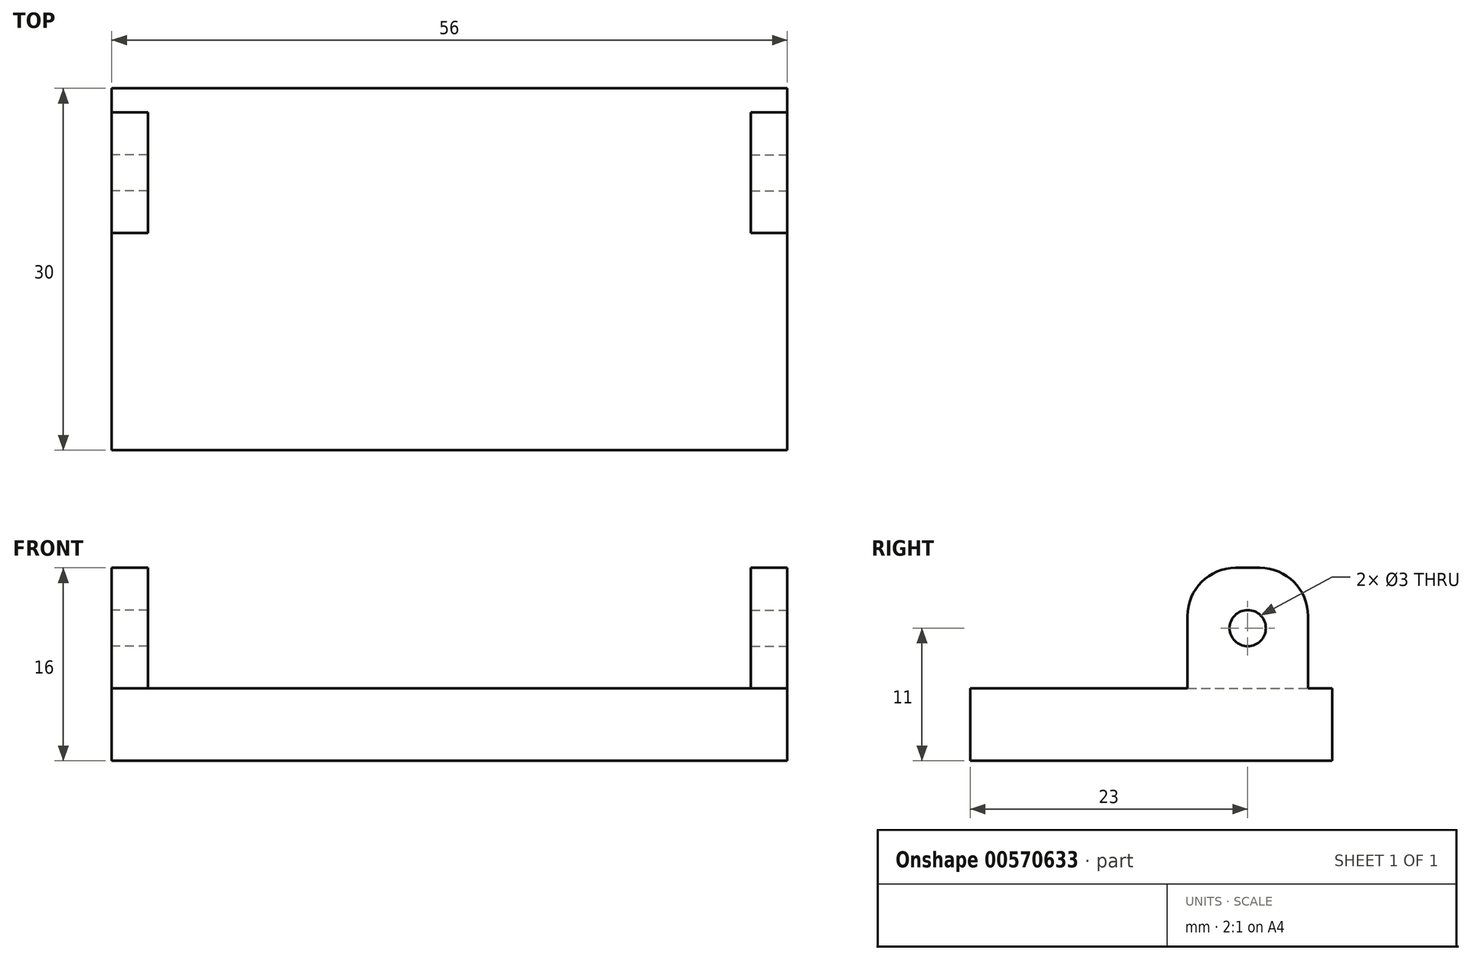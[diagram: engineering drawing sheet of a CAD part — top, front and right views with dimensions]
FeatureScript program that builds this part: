
annotation { "Feature Type Name" : "Feature", "Feature Type Description" : "" }
export const myFeature = defineFeature(function(context is Context, id is Id, definition is map)
    precondition{}
    {
        {
            var Q0;
            Q0=qCreatedBy(makeId("Top.planeOp"),FACE);
            var sketch = newSketch(context, id + "F0", { "sketchPlane" : qUnion([Q0])});
            skLineSegment(sketch, "E0.bottom", {"start": v(14, -15) * mm, "end": v(-14, -15) * mm});
            skLineSegment(sketch, "E0.top", {"start": v(14, 15) * mm, "end": v(-14, 15) * mm});
            skLineSegment(sketch, "E0.left", {"start": v(14, -15) * mm, "end": v(14, 15) * mm});
            skLineSegment(sketch, "E0.right", {"start": v(-14, -15) * mm, "end": v(-14, 15) * mm});
            skPoint(sketch, "E0.middle", {"position": v(0, 0) * mm});
            skSolve(sketch);
        }
        {
            var Q0;
            Q0 = qSketchRegion(id + "F0", true);
            extrude(context, id + "F1", {"entities" : qUnion([Q0]), "depth" : 6 * mm, "offsetDistance" : 25 * mm});
        }
        {
            var Q0;
            Q0=makeQuery(id+"F1.opExtrude","SWEPT_FACE",FACE,{"disambiguationData":[OSD([sQuery(id+"F0.wireOp",EDGE,"E0.left")])]});
            var sketch = newSketch(context, id + "F2", { "sketchPlane" : qUnion([Q0])});
            skLineSegment(sketch, "E1.bottom", {"start": v(13, 6) * mm, "end": v(3, 6) * mm});
            skLineSegment(sketch, "E1.top", {"start": v(9, 16) * mm, "end": v(7, 16) * mm});
            skLineSegment(sketch, "E1.left", {"start": v(13, 6) * mm, "end": v(13, 12) * mm});
            skLineSegment(sketch, "E1.right", {"start": v(3, 6) * mm, "end": v(3, 12) * mm});
            skCircle(sketch, "E2", {"center": v(8, 11) * mm, "radius": 1.5 * mm});
            skPoint(sketch, "E2.centerSnap0", {"position": v(8, 6) * mm});
            skPoint(sketch, "E3.visualSharp", {"position": v(3, 16) * mm});
            skArc(sketch, "E3.filletArc", {"start": v(7, 16) * mm, "mid": v(4.17, 14.83) * mm, "end": v(3, 12) * mm});
            skPoint(sketch, "E4.visualSharp", {"position": v(13, 16) * mm});
            skArc(sketch, "E4.filletArc", {"start": v(13, 12) * mm, "mid": v(11.83, 14.83) * mm, "end": v(9, 16) * mm});
            skSolve(sketch);
        }
        {
            var Q0;
            Q0 = qSketchRegion(id + "F2", true);
            extrude(context, id + "F3", {"entities" : qUnion([Q0]), "oppositeDirection" : true, "depth" : 3 * mm, "offsetDistance" : 25 * mm});
        }
        {
            var Q0;
            Q0=makeQuery(id+"F3.opExtrude","SWEPT_BODY",BODY,{"disambiguationData":[OSD([sQuery(id+"F2.wireOp",EDGE,"E1.bottom"),sQuery(id+"F2.wireOp",EDGE,"E1.top"),sQuery(id+"F2.wireOp",EDGE,"E1.left"),sQuery(id+"F2.wireOp",EDGE,"E1.right"),sQuery(id+"F2.wireOp",EDGE,"E2"),sQuery(id+"F2.wireOp",EDGE,"E3.filletArc"),sQuery(id+"F2.wireOp",EDGE,"E4.filletArc")])]});
            var Q1;
            Q1=makeQuery(id+"F1.opExtrude","SWEPT_BODY",BODY,{"disambiguationData":[OSD([sQuery(id+"F0.wireOp",EDGE,"E0.bottom"),sQuery(id+"F0.wireOp",EDGE,"E0.top"),sQuery(id+"F0.wireOp",EDGE,"E0.left"),sQuery(id+"F0.wireOp",EDGE,"E0.right")])]});
            var Q2;
            Q2=makeQuery(id+"F1.opExtrude","SWEPT_FACE",FACE,{"disambiguationData":[OSD([sQuery(id+"F0.wireOp",EDGE,"E0.right")])]});
            mirror(context, id + "F4", {"operationType" : NewBodyOperationType.ADD, "entities" : qUnion([Q0, Q1]), "mirrorPlane" : qUnion([Q2])});
        }
    });
